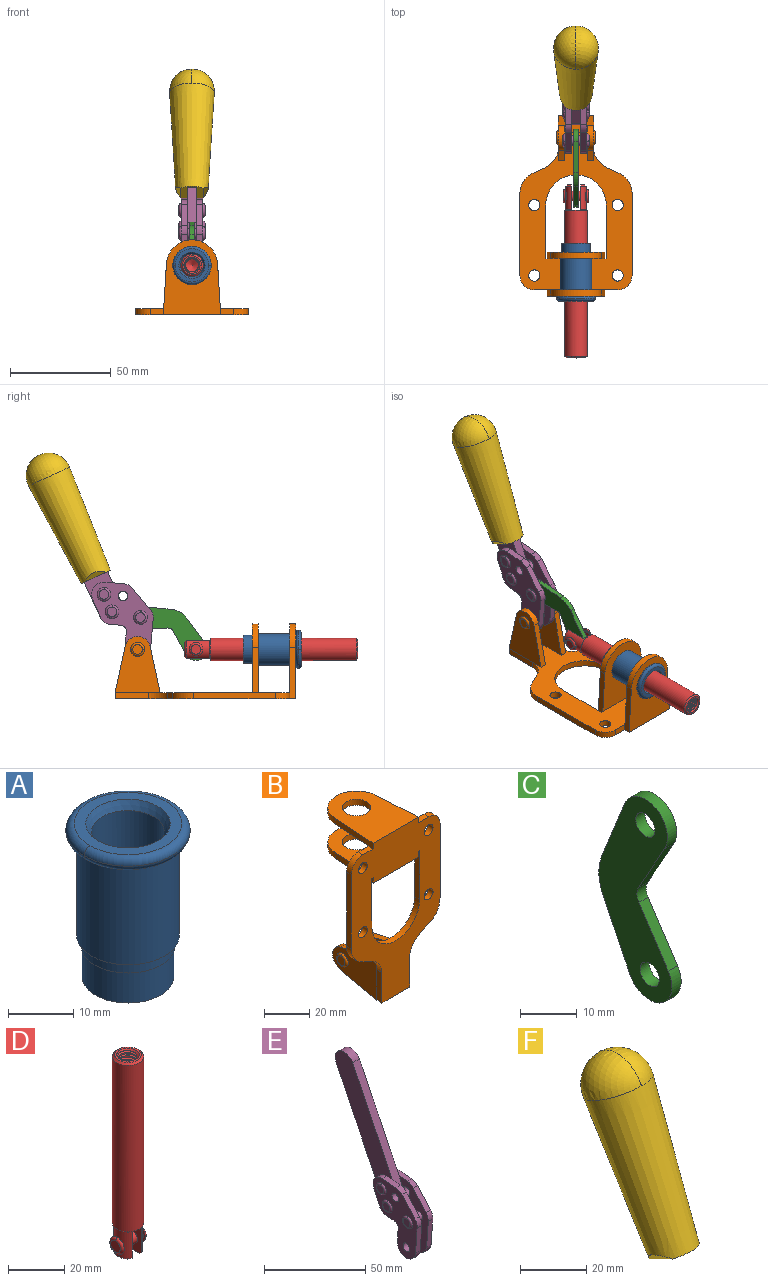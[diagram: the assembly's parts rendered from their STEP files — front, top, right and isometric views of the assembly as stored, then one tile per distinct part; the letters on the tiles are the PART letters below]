
ASSEMBLY  parts=6 mates=6
PART A: 15 faces, bbox 20.6x20.6x28.7 mm
  f0: torus R=8.26mm, axis (0,0,1), area 56.8mm2, adj f1,f10,f12
  f1: torus R=8.26mm, axis (0,0,1), area 56.8mm2, adj f0,f6,f13
  f2: cylinder r=5.59mm len=25.91mm, axis (0,0,1), area 909.6mm2, adj f3,f4
  f3: cone r=6.86mm half-angle=45deg, axis (0,0,-1), area 70.2mm2, adj f2,f14
  f4: cone r=6.47mm half-angle=30deg, axis (0,0,1), area 66.7mm2, adj f2,f13
  f5: cylinder r=7.04mm len=14.07mm, axis (0,0,1), area 252.6mm2, adj f11,f14
  f6: torus R=8.26mm, axis (0,0,1), area 56.8mm2, adj f1,f12,f13
  f7: cylinder r=7.16mm len=14.33mm, axis (0,0,1), area 91.5mm2, adj f9,f11
  f8: cylinder r=7.86mm len=18.42mm, axis (0,0,1), area 909.6mm2, adj f9,f10
  f9: plane 15.72x15.72mm, normal (0,0,-1), area 33mm2, adj f7,f8
  f10: plane 16.51x16.51mm, normal (0,0,-1), area 19.9mm2, adj f0,f8,f12
  f11: plane 14.33x14.33mm, normal (0,0,-1), area 5.7mm2, adj f5,f7
  f12: torus R=8.26mm, axis (0,0,1), area 56.8mm2, adj f0,f6,f10
  f13: plane 16.51x16.51mm, normal (0,0,1), area 82.7mm2, adj f1,f4,f6
  f14: plane 14.07x14.07mm, normal (0,0,-1), area 7.8mm2, adj f3,f5
PART B: 55 faces, bbox 55.7x37.4x89.8 mm
  f0: torus R=2.41mm, axis (-1,0,0), area 15mm2, adj f11,f15,f25
  f1: torus R=2.41mm, axis (-1,0,0), area 15mm2, adj f10,f12,f22
  f2: cylinder r=2.78mm len=5.56mm, axis (0,-1,0), area 54.2mm2, adj f30,f54
  f3: cylinder r=14.99mm len=29.97mm, axis (0,-1,0), area 145.9mm2, adj f30,f49,f53,f54
  f4: cylinder r=2.78mm len=5.56mm, axis (0,-1,0), area 54.2mm2, adj f30,f54
  f5: cylinder r=2.78mm len=5.56mm, axis (0,-1,0), area 54.2mm2, adj f30,f54
  f6: cylinder r=2.78mm len=5.56mm, axis (0,-1,0), area 54.2mm2, adj f30,f54
  f7: cylinder r=6.35mm len=12.7mm, axis (0,0,1), area 123.6mm2, adj f27,f51
  f8: cylinder r=6.35mm len=12.7mm, axis (0,0,-1), area 124.7mm2, adj f21,f35
  f9: cylinder r=2.41mm len=11.18mm, axis (-1,0,0), area 169.4mm2, adj f16,f19
  f10: plane 4.83x4.83mm, normal (1,0,0), area 18.3mm2, adj f1,f12
  f11: plane 4.83x4.83mm, normal (-1,0,0), area 18.3mm2, adj f0,f15
  f12: torus R=2.41mm, axis (-1,0,0), area 15mm2, adj f1,f10,f22
  f13: cylinder r=6.35mm len=12.41mm, axis (1,0,0), area 53.4mm2, adj f18,f19,f22,f23
  f14: cylinder r=6.35mm len=12.41mm, axis (-1,0,0), area 53.4mm2, adj f16,f17,f24,f25
  f15: torus R=2.41mm, axis (-1,0,0), area 15mm2, adj f0,f11,f25
  f16: plane 27.86x22.35mm, normal (1,0,0), area 425.4mm2, adj f9,f14,f17,f24,f30
  f17: plane 22.86x4.97mm, normal (0,0.21,0.98), area 72.5mm2, adj f14,f16,f25,f30
  f18: plane 22.86x4.97mm, normal (0,0.21,0.98), area 72.5mm2, adj f13,f19,f22,f30
  f19: plane 27.86x22.35mm, normal (-1,0,0), area 425.4mm2, adj f9,f13,f18,f23,f30
  f20: cylinder r=12.7mm len=25.35mm, axis (0,0,-1), area 119.8mm2, adj f21,f34,f35,f36
  f21: plane 34.21x28.07mm, normal (0,0,-1), area 702.4mm2, adj f8,f20,f30,f34,f36
  f22: plane 27.96x22.45mm, normal (1,0,0), area 407.2mm2, adj f1,f12,f13,f18,f23,f30,f42,f43
  f23: plane 22.86x4.97mm, normal (0,0.21,-0.98), area 72.5mm2, adj f13,f19,f22,f44
  f24: plane 22.86x4.97mm, normal (0,0.21,-0.98), area 72.5mm2, adj f14,f16,f25,f44
  f25: plane 27.86x22.35mm, normal (-1,0,0), area 407.1mm2, adj f0,f14,f15,f17,f24,f30,f45,f46
  f26: plane 3.1x0.95mm, normal (0,0,-1), area 2.7mm2, adj f30,f49,f50,f54
  f27: plane 34.21x28.07mm, normal (0,0,1), area 702.4mm2, adj f7,f28,f30,f50,f52
  f28: cylinder r=12.7mm len=25.35mm, axis (0,0,1), area 118.8mm2, adj f27,f50,f51,f52
  f29: plane 3.1x0.95mm, normal (0,0,-1), area 2.7mm2, adj f30,f52,f53,f54
  f30: plane 86.54x55.63mm, normal (0,1,0), area 2362.9mm2, adj f2,f3,f4,f5,f6,f16,f17,f18
  f31: plane 40.56x3.1mm, normal (-1,0,0), area 125.7mm2, adj f30,f32,f48,f54
  f32: cylinder r=7.11mm len=7.11mm, axis (0,-1,0), area 34.6mm2, adj f30,f31,f33,f54
  f33: plane 6.67x3.1mm, normal (0,0,1), area 20.4mm2, adj f30,f32,f34,f54
  f34: plane 25.39x3.13mm, normal (-1,0.06,0), area 79.5mm2, adj f20,f21,f33,f35,f54
  f35: plane 37.31x28.45mm, normal (0,0,1), area 789.9mm2, adj f8,f20,f34,f36,f54
  f36: plane 25.39x3.13mm, normal (1,0.06,0), area 79.5mm2, adj f20,f21,f35,f37,f54
  f37: plane 6.67x3.1mm, normal (0,0,1), area 20.4mm2, adj f30,f36,f38,f54
  f38: cylinder r=7.11mm len=7.11mm, axis (0,-1,0), area 34.6mm2, adj f30,f37,f39,f54
  f39: plane 40.56x3.1mm, normal (1,0,0), area 125.7mm2, adj f30,f38,f40,f54
  f40: cylinder r=11.18mm len=10.16mm, axis (0,-1,0), area 39.5mm2, adj f30,f39,f41,f54
  f41: plane 6.09x3.1mm, normal (0.42,0,-0.91), area 20.8mm2, adj f30,f40,f42,f54
  f42: cylinder r=11.18mm len=9.41mm, axis (0,-1,0), area 37.2mm2, adj f22,f30,f41,f43,f54
  f43: plane 16.5x3.1mm, normal (1,0,0), area 51.1mm2, adj f22,f42,f44,f54
  f44: plane 17.37x3.1mm, normal (0,0,-1), area 53.8mm2, adj f23,f24,f30,f43,f45,f54
  f45: plane 16.5x3.1mm, normal (-1,0,0), area 51.1mm2, adj f25,f44,f46,f54
  f46: cylinder r=11.18mm len=9.41mm, axis (0,-1,0), area 37.2mm2, adj f25,f30,f45,f47,f54
  f47: plane 6.09x3.1mm, normal (-0.42,0,-0.91), area 20.8mm2, adj f30,f46,f48,f54
  f48: cylinder r=11.18mm len=10.16mm, axis (0,-1,0), area 39.5mm2, adj f30,f31,f47,f54
  f49: plane 26.54x3.1mm, normal (-1,0,0), area 82.3mm2, adj f3,f26,f30,f54
  f50: plane 25.39x3.1mm, normal (1,0.06,0), area 78.8mm2, adj f26,f27,f28,f51,f54
  f51: plane 37.31x28.45mm, normal (0,0,-1), area 789.9mm2, adj f7,f28,f50,f52,f54
  f52: plane 25.39x3.1mm, normal (-1,0.06,0), area 78.8mm2, adj f27,f28,f29,f51,f54
  f53: plane 26.54x3.1mm, normal (1,0,0), area 82.3mm2, adj f3,f29,f30,f54
  f54: plane 89.66x55.63mm, normal (0,-1,0), area 2678.5mm2, adj f2,f3,f4,f5,f6,f26,f29,f31
PART C: 12 faces, bbox 2.3x18.2x42.8 mm
  f0: cylinder r=2.4mm len=4.8mm, axis (1,0,0), area 34.9mm2, adj f4,f11
  f1: cylinder r=10.41mm len=8.47mm, axis (1,0,0), area 20.2mm2, adj f4,f9,f10,f11
  f2: cylinder r=3.05mm len=3.16mm, axis (1,0,0), area 7.7mm2, adj f4,f6,f7,f11
  f3: cylinder r=2.4mm len=4.8mm, axis (1,0,0), area 34.9mm2, adj f4,f11
  f4: plane 42.81x18.23mm, normal (-1,0,0), area 414.1mm2, adj f0,f1,f2,f3,f5,f6,f7,f8
  f5: cylinder r=5.54mm len=10.67mm, axis (1,0,0), area 41.8mm2, adj f4,f6,f10,f11
  f6: plane 11.66x6.53mm, normal (0,-0.87,-0.49), area 30.9mm2, adj f2,f4,f5,f11
  f7: plane 11.17x7.33mm, normal (0,-0.84,0.55), area 30.9mm2, adj f2,f4,f8,f11
  f8: cylinder r=5.54mm len=10.51mm, axis (1,0,0), area 41.8mm2, adj f4,f7,f9,f11
  f9: plane 13.67x6.67mm, normal (0,0.9,-0.44), area 35.1mm2, adj f1,f4,f8,f11
  f10: plane 14.1x5.7mm, normal (0,0.93,0.37), area 35.1mm2, adj f1,f4,f5,f11
  f11: plane 42.81x18.23mm, normal (1,0,0), area 414.1mm2, adj f0,f1,f2,f3,f5,f6,f7,f8
PART D: 48 faces, bbox 12.6x11.1x86.1 mm
  f0: torus R=2.41mm, axis (-1,0,0), area 15mm2, adj f30,f32,f34
  f1: torus R=2.41mm, axis (-1,0,0), area 15mm2, adj f29,f31,f33
  f2: cylinder r=5.54mm len=72.39mm, axis (0,0,1), area 2518.5mm2, adj f3,f4,f42,f43
  f3: cone r=5.54mm half-angle=45deg, axis (0,0,1), area 7.6mm2, adj f2,f5,f41
  f4: cone r=5.54mm half-angle=45deg, axis (0,0,-1), area 34.9mm2, adj f2,f39
  f5: cylinder r=5.08mm len=11.48mm, axis (0,0,1), area 108.3mm2, adj f3,f7,f8,f41
  f6: cylinder r=2.41mm len=4.83mm, axis (-1,0,0), area 71.2mm2, adj f40,f41
  f7: cylinder r=2.41mm len=4.83mm, axis (-1,0,0), area 7.6mm2, adj f5,f34
  f8: cone r=5.08mm half-angle=45deg, axis (0,0,1), area 10.6mm2, adj f5,f37,f41
  f9: cone r=3.98mm half-angle=45deg, axis (0,0,1), area 17.6mm2, adj f27,f39,f45,f46,f47
  f10: cylinder r=2.41mm len=4.83mm, axis (-1,0,0), area 7.6mm2, adj f33,f38
  f11: cylinder r=3.2mm len=6.4mm, axis (0,0,1), area 78.4mm2, adj f12,f28,f44,f45,f47
  f12: cylinder r=3.2mm len=6.4mm, axis (0,0,1), area 10.5mm2, adj f11,f13,f45,f47
  f13: cylinder r=3.2mm len=6.4mm, axis (0,0,1), area 10.5mm2, adj f12,f14,f45,f47
  f14: cylinder r=3.2mm len=6.4mm, axis (0,0,1), area 10.5mm2, adj f13,f15,f45,f47
  f15: cylinder r=3.2mm len=6.4mm, axis (0,0,1), area 10.5mm2, adj f14,f16,f45,f47
  f16: cylinder r=3.2mm len=6.4mm, axis (0,0,1), area 10.5mm2, adj f15,f17,f45,f47
  f17: cylinder r=3.2mm len=6.4mm, axis (0,0,1), area 10.5mm2, adj f16,f18,f45,f47
  f18: cylinder r=3.2mm len=6.4mm, axis (0,0,1), area 10.5mm2, adj f17,f19,f45,f47
  f19: cylinder r=3.2mm len=6.4mm, axis (0,0,1), area 10.5mm2, adj f18,f20,f45,f47
  f20: cylinder r=3.2mm len=6.4mm, axis (0,0,1), area 10.5mm2, adj f19,f21,f45,f47
  f21: cylinder r=3.2mm len=6.4mm, axis (0,0,1), area 10.5mm2, adj f20,f22,f45,f47
  f22: cylinder r=3.2mm len=6.4mm, axis (0,0,1), area 10.5mm2, adj f21,f23,f45,f47
  f23: cylinder r=3.2mm len=6.4mm, axis (0,0,1), area 10.5mm2, adj f22,f24,f45,f47
  f24: cylinder r=3.2mm len=6.4mm, axis (0,0,1), area 10.5mm2, adj f23,f25,f45,f47
  f25: cylinder r=3.2mm len=6.4mm, axis (0,0,1), area 10.5mm2, adj f24,f26,f45,f47
  f26: cylinder r=3.2mm len=6.4mm, axis (0,0,1), area 10.5mm2, adj f25,f27,f45,f47
  f27: cylinder r=3.2mm len=6.4mm, axis (0,0,1), area 7.4mm2, adj f9,f26,f45,f47
  f28: cone r=3.2mm half-angle=60deg, axis (0,0,1), area 37.2mm2, adj f11
  f29: plane 4.83x4.83mm, normal (-1,0,0), area 18.3mm2, adj f1,f31
  f30: plane 4.83x4.83mm, normal (1,0,0), area 18.3mm2, adj f0,f32
  f31: torus R=2.41mm, axis (-1,0,0), area 15mm2, adj f1,f29,f33
  f32: torus R=2.41mm, axis (-1,0,0), area 15mm2, adj f0,f30,f34
  f33: plane 6.83x6.83mm, normal (1,0,0), area 18.3mm2, adj f1,f10,f31
  f34: plane 6.83x6.83mm, normal (-1,0,0), area 18.3mm2, adj f0,f7,f32
  f35: cone r=5.08mm half-angle=45deg, axis (0,0,1), area 10.6mm2, adj f36,f38,f40
  f36: plane 7.25x1.97mm, normal (0,0,-1), area 10mm2, adj f35,f40
  f37: plane 7.25x1.97mm, normal (0,0,-1), area 10mm2, adj f8,f41
  f38: cylinder r=5.08mm len=11.48mm, axis (0,0,1), area 108.3mm2, adj f10,f35,f40,f42
  f39: plane 9.55x9.55mm, normal (0,0,1), area 22mm2, adj f4,f9
  f40: plane 12.76x10.09mm, normal (1,0,0), area 95.7mm2, adj f6,f35,f36,f38,f42,f43
  f41: plane 12.76x10.09mm, normal (-1,0,0), area 95.7mm2, adj f3,f5,f6,f8,f37,f43
  f42: cone r=5.54mm half-angle=45deg, axis (0,0,1), area 7.6mm2, adj f2,f38,f40
  f43: plane 11.07x4.7mm, normal (0,0,-1), area 50.4mm2, adj f2,f40,f41
  f44: plane 0.89x0.62mm, normal (-1,0,0), area 0.3mm2, adj f11,f45,f46,f47
  f45: bspline ~24.8x7.63mm, area 266.6mm2, adj f9,f11,f12,f13,f14,f15,f16,f17
  f46: bspline ~24.87x7.63mm, area 73.6mm2, adj f9,f44,f45,f47
  f47: bspline ~24.98x7.63mm, area 272.5mm2, adj f9,f11,f12,f13,f14,f15,f16,f17
PART E: 59 faces, bbox 12.9x60.2x99.6 mm
  f0: torus R=2.39mm, axis (-1,0,0), area 14.9mm2, adj f20,f43,f51
  f1: torus R=2.39mm, axis (-1,0,0), area 14.9mm2, adj f19,f42,f51
  f2: torus R=2.39mm, axis (-1,0,0), area 14.9mm2, adj f18,f35,f51
  f3: torus R=2.39mm, axis (-1,0,0), area 14.9mm2, adj f14,f17,f23
  f4: torus R=2.39mm, axis (-1,0,0), area 14.9mm2, adj f13,f16,f23
  f5: torus R=2.39mm, axis (-1,0,0), area 14.9mm2, adj f12,f15,f23
  f6: cylinder r=2.39mm len=4.78mm, axis (1,0,0), area 46.5mm2, adj f48,f50,f51
  f7: cylinder r=2.39mm len=4.78mm, axis (1,0,0), area 46.5mm2, adj f50,f51
  f8: cylinder r=6.35mm len=12.68mm, axis (1,0,0), area 61.8mm2, adj f38,f39,f50,f51
  f9: cylinder r=2.39mm len=4.78mm, axis (-1,0,0), area 70.5mm2, adj f46,f50
  f10: cylinder r=2.39mm len=4.78mm, axis (-1,0,0), area 46.5mm2, adj f23,f45,f46
  f11: cylinder r=2.39mm len=4.78mm, axis (-1,0,0), area 46.5mm2, adj f23,f46
  f12: plane 4.78x4.78mm, normal (1,0,0), area 17.9mm2, adj f5,f15
  f13: plane 4.78x4.78mm, normal (1,0,0), area 17.9mm2, adj f4,f16
  f14: plane 4.78x4.78mm, normal (1,0,0), area 17.9mm2, adj f3,f17
  f15: torus R=2.39mm, axis (-1,0,0), area 14.9mm2, adj f5,f12,f23
  f16: torus R=2.39mm, axis (-1,0,0), area 14.9mm2, adj f4,f13,f23
  f17: torus R=2.39mm, axis (-1,0,0), area 14.9mm2, adj f3,f14,f23
  f18: plane 4.78x4.78mm, normal (-1,0,0), area 17.9mm2, adj f2,f35
  f19: plane 4.78x4.78mm, normal (-1,0,0), area 17.9mm2, adj f1,f42
  f20: plane 4.78x4.78mm, normal (-1,0,0), area 17.9mm2, adj f0,f43
  f21: plane 2.26x0.2mm, normal (1,0,0), area 0.2mm2, adj f31,f44
  f22: plane 2.26x0.2mm, normal (-1,0,0), area 0.2mm2, adj f41,f44
  f23: plane 39.37x30.77mm, normal (1,0,0), area 565.5mm2, adj f3,f4,f5,f10,f11,f15,f16,f17
  f24: cylinder r=6.1mm len=4.15mm, axis (-1,0,0), area 14.7mm2, adj f23,f25,f32,f46
  f25: plane 10.25x9.01mm, normal (0,-0.75,0.66), area 42.3mm2, adj f23,f24,f26,f46
  f26: cylinder r=6.35mm len=4.64mm, axis (-1,0,0), area 15.6mm2, adj f23,f25,f27,f46
  f27: plane 15.84x3.1mm, normal (0,-1,-0.07), area 49.2mm2, adj f23,f26,f28,f46
  f28: cylinder r=6.35mm len=12.68mm, axis (-1,0,0), area 61.8mm2, adj f23,f27,f29,f46
  f29: plane 8.11x3.1mm, normal (0,1,0.07), area 25.2mm2, adj f23,f28,f30,f46
  f30: cylinder r=3.05mm len=3.25mm, axis (-1,0,0), area 14.8mm2, adj f23,f29,f31,f46
  f31: plane 5.99x3.1mm, normal (0,0.07,-1), area 18.6mm2, adj f21,f23,f30,f44,f46
  f32: plane 9.5x3.1mm, normal (0,-0.07,1), area 29.5mm2, adj f23,f24,f33,f46,f47
  f33: cylinder r=6.1mm len=8.63mm, axis (-1,0,0), area 39.1mm2, adj f23,f32,f34,f47
  f34: plane 8.65x3.96mm, normal (0,0.91,-0.42), area 29.5mm2, adj f23,f33,f44,f47
  f35: torus R=2.39mm, axis (-1,0,0), area 14.9mm2, adj f2,f18,f51
  f36: plane 10.25x9.01mm, normal (0,-0.75,0.66), area 42.3mm2, adj f37,f49,f50,f51
  f37: cylinder r=6.35mm len=4.64mm, axis (1,0,0), area 15.6mm2, adj f36,f38,f50,f51
  f38: plane 15.84x3.1mm, normal (0,-1,-0.07), area 49.2mm2, adj f8,f37,f50,f51
  f39: plane 8.11x3.1mm, normal (0,1,0.07), area 25.2mm2, adj f8,f40,f50,f51
  f40: cylinder r=3.05mm len=3.25mm, axis (1,0,0), area 14.8mm2, adj f39,f41,f50,f51
  f41: plane 5.99x3.1mm, normal (0,0.07,-1), area 18.6mm2, adj f22,f40,f44,f50,f51
  f42: torus R=2.39mm, axis (-1,0,0), area 14.9mm2, adj f1,f19,f51
  f43: torus R=2.39mm, axis (-1,0,0), area 14.9mm2, adj f0,f20,f51
  f44: cylinder r=6.35mm len=12.12mm, axis (-1,0,0), area 128.9mm2, adj f21,f22,f23,f31,f34,f41,f46,f47
  f45: plane 2.65x1.35mm, normal (1,0,0), area 1mm2, adj f10,f55
  f46: plane 39.08x20.42mm, normal (-1,0,0), area 412.5mm2, adj f9,f10,f11,f24,f25,f26,f27,f28
  f47: plane 77.62x39.82mm, normal (1,0,0), area 850mm2, adj f32,f33,f34,f44,f53,f54,f55
  f48: plane 2.65x1.35mm, normal (-1,0,0), area 1mm2, adj f6,f55
  f49: cylinder r=6.1mm len=4.15mm, axis (1,0,0), area 14.7mm2, adj f36,f50,f51,f56
  f50: plane 39.08x20.42mm, normal (1,0,0), area 412.5mm2, adj f6,f7,f8,f9,f36,f37,f38,f39
  f51: plane 39.37x30.77mm, normal (-1,0,0), area 565.5mm2, adj f0,f1,f2,f6,f7,f8,f35,f36
  f52: plane 8.65x3.96mm, normal (0,0.91,-0.42), area 29.5mm2, adj f44,f51,f57,f58
  f53: plane 68.49x33.4mm, normal (0,0.9,-0.44), area 358.1mm2, adj f44,f47,f54,f58
  f54: cylinder r=6.35mm len=12.06mm, axis (1,0,0), area 93.7mm2, adj f47,f53,f55,f58
  f55: plane 68.49x33.4mm, normal (0,-0.9,0.44), area 358.1mm2, adj f44,f45,f46,f47,f48,f50,f54,f58
  f56: plane 9.5x3.1mm, normal (0,-0.07,1), area 29.5mm2, adj f49,f50,f51,f57,f58
  f57: cylinder r=6.1mm len=8.63mm, axis (1,0,0), area 39.1mm2, adj f51,f52,f56,f58
  f58: plane 77.62x39.82mm, normal (-1,0,0), area 850mm2, adj f44,f52,f53,f54,f55,f56,f57
PART F: 11 faces, bbox 22.3x42.6x64.5 mm
  f0: sphere r=11.13mm, area 411.4mm2, adj f1,f8
  f1: cone r=11.11mm half-angle=3.3deg, axis (0,0.44,0.9), area 3251.8mm2, adj f0,f7,f8,f9,f10
  f2: cylinder r=6.16mm len=11.7mm, axis (1,0,0), area 89.5mm2, adj f3,f4,f5,f6
  f3: plane 60.23x36.75mm, normal (-1,0,0), area 763.6mm2, adj f2,f4,f6,f10
  f4: plane 51.37x25.05mm, normal (0,0.9,-0.44), area 264.2mm2, adj f2,f3,f5,f10
  f5: plane 60.23x36.75mm, normal (1,0,0), area 763.6mm2, adj f2,f4,f6,f10
  f6: plane 51.37x25.05mm, normal (0,-0.9,0.44), area 264.2mm2, adj f2,f3,f5,f10
  f7: plane 9.95x5.95mm, normal (0.71,-0.31,-0.64), area 25.8mm2, adj f1,f10
  f8: sphere r=11.13mm, area 411.4mm2, adj f0,f1
  f9: plane 9.95x5.95mm, normal (-0.71,-0.31,-0.64), area 25.8mm2, adj f1,f10
  f10: plane 14.27x11.38mm, normal (0,-0.44,-0.9), area 106.7mm2, adj f1,f3,f4,f5,f6,f7,f9
PLACE A rot(axis=(1,0,0),90deg) t=(0,9.43,0)mm
PLACE B rot(axis=(1,0,0),90deg) t=(0,9.43,0)mm fixed
PLACE C rot(axis=(1,0,0),121.9deg) t=(0,38.73,11.88)mm
PLACE D rot(axis=(1,0,0),90deg) t=(0,28.07,0)mm
PLACE E rot(axis=(1,0,0),1deg) t=(0,16.33,56.25)mm
PLACE F rot(axis=(1,0,0),1deg) t=(-0.04,16.33,56.25)mm
MATE fastened B.f7 <-> A.f2  axis (0,-1,0) through (0,-36.96,24.61)mm
MATE revolute E.f7 <-> B.f0  axis (1,0,0) through (0,41.52,24.61)mm
MATE slider D.f2 <-> A.f2  axis (0,-1,0) through (0,-30.71,24.61)mm
MATE revolute C.f3 <-> E.f4  axis (1,0,0) through (0,40.13,40.43)mm
MATE fastened F.f2 <-> E.f54  axis (1,0,0) through (-2.35,86.36,112.31)mm
MATE revolute D.f6 <-> C.f5  axis (-1,0,0) through (0,12.59,24.61)mm
